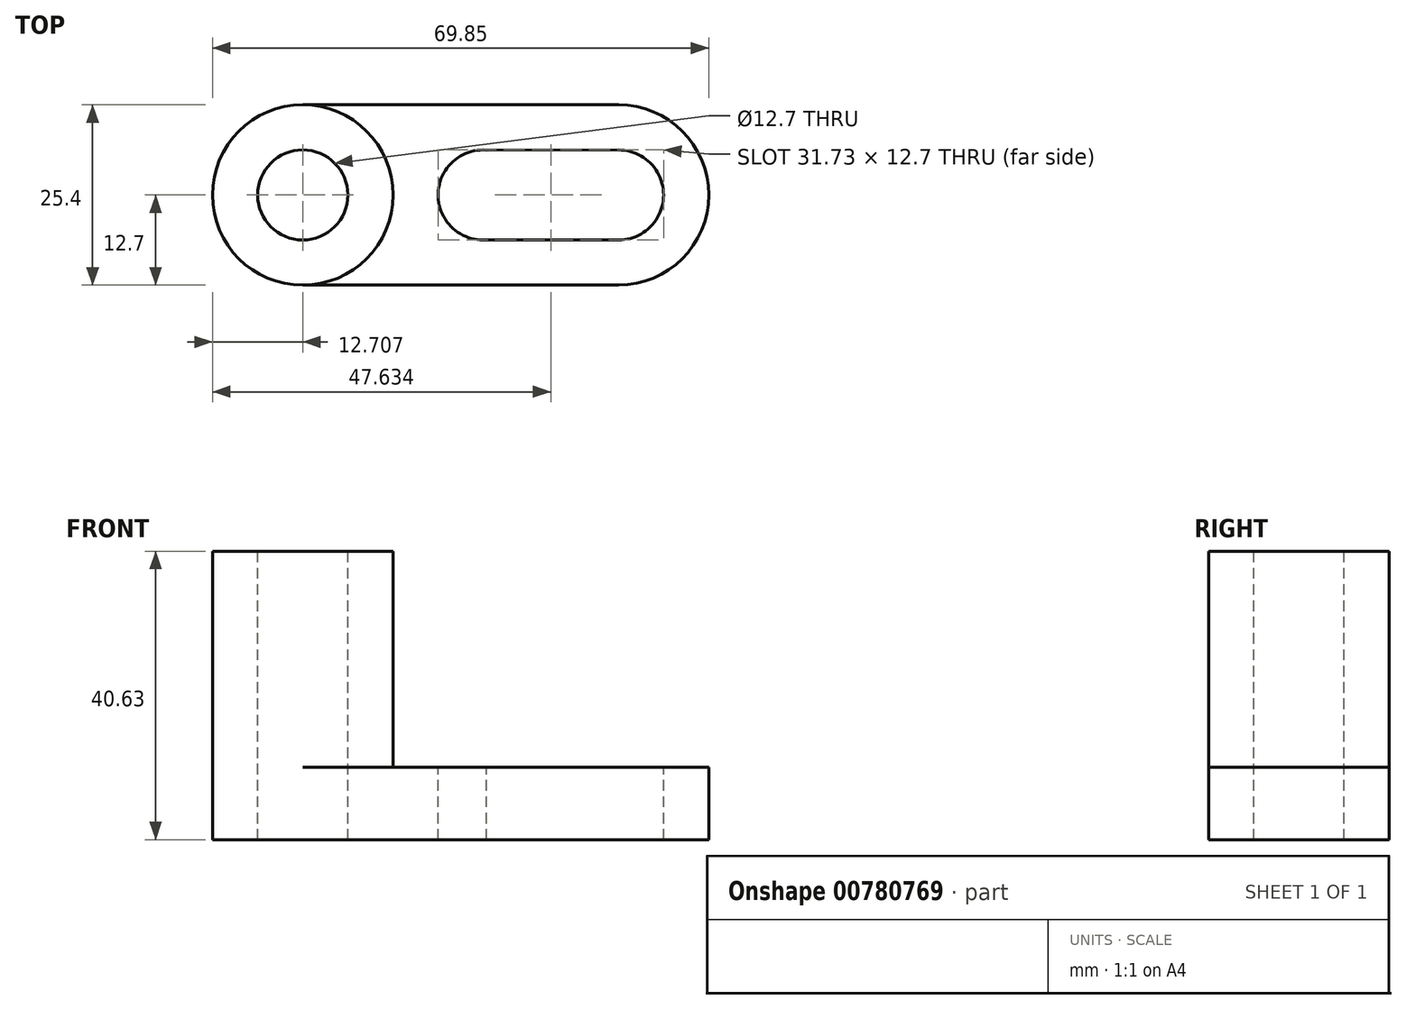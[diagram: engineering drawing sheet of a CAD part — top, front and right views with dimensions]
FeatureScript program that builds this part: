
annotation { "Feature Type Name" : "Feature", "Feature Type Description" : "" }
export const myFeature = defineFeature(function(context is Context, id is Id, definition is map)
    precondition{}
    {
        {
            var Q0;
            Q0=qCreatedBy(makeId("Front.planeOp"),FACE);
            var sketch = newSketch(context, id + "F0", { "sketchPlane" : qUnion([Q0])});
            skLineSegment(sketch, "E0", {"start": v(0, 0) * mm, "end": v(69.85, 0) * mm});
            skLineSegment(sketch, "E1", {"start": v(69.85, 0) * mm, "end": v(69.85, 10.2) * mm});
            skLineSegment(sketch, "E2", {"start": v(69.85, 10.2) * mm, "end": v(25.41, 10.2) * mm});
            skLineSegment(sketch, "E3", {"start": v(25.41, 10.2) * mm, "end": v(25.41, 40.63) * mm});
            skLineSegment(sketch, "E4", {"start": v(25.41, 40.63) * mm, "end": v(0, 40.63) * mm});
            skLineSegment(sketch, "E5", {"start": v(0, 40.63) * mm, "end": v(0, 0) * mm});
            skSolve(sketch);
        }
        {
            var Q0;
            Q0=makeQuery(id+"F0.imprint","IMPRINT",FACE,{"disambiguationData":[TD([[makeQuery(id+"F0.imprint","IMPRINT",EDGE,{"derivedFrom":sQuery(id+"F0.wireOp",EDGE,"E0")}),1.0]])]});
            extrude(context, id + "F1", {"entities" : qUnion([Q0]), "depth" : 25.4 * mm, "offsetDistance" : 25.4 * mm});
        }
        {
            var Q0;
            Q0=makeQuery(id+"F1.opExtrude","SWEPT_FACE",FACE,{"disambiguationData":[OSD([sQuery(id+"F0.wireOp",EDGE,"E4")])]});
            var sketch = newSketch(context, id + "F2", { "sketchPlane" : qUnion([Q0])});
            skCircle(sketch, "E6", {"center": v(12.7, -12.7) * mm, "radius": 6.35 * mm});
            skPoint(sketch, "E6.centerSnap0", {"position": v(0, -12.7) * mm});
            skPoint(sketch, "E6.centerSnap1", {"position": v(12.7, -25.4) * mm});
            skSolve(sketch);
        }
        {
            var Q0;
            Q0=makeQuery(id+"F2.imprint","IMPRINT",FACE,{"disambiguationData":[TD([[makeQuery(id+"F2.imprint","IMPRINT",EDGE,{"derivedFrom":sQuery(id+"F2.wireOp",EDGE,"E6")}),1.0]])]});
            extrude(context, id + "F3", {"entities" : qUnion([Q0]), "operationType" : NewBodyOperationType.REMOVE, "oppositeDirection" : true, "depth" : 50.8 * mm, "offsetDistance" : 25.4 * mm});
        }
        {
            var Q0;
            Q0=makeQuery(id+"F1.opExtrude","CAP_EDGE",EDGE,{"disambiguationData":[OSD([sQuery(id+"F0.wireOp",EDGE,"E3")])],"isStart":false});
            var Q1;
            Q1=makeQuery(id+"F1.opExtrude","CAP_EDGE",EDGE,{"disambiguationData":[OSD([sQuery(id+"F0.wireOp",EDGE,"E3")])],"isStart":true});
            var Q2;
            Q2=makeQuery(id+"F1.opExtrude","CAP_EDGE",EDGE,{"disambiguationData":[OSD([sQuery(id+"F0.wireOp",EDGE,"E5")])],"isStart":false});
            var Q3;
            Q3=makeQuery(id+"F1.opExtrude","CAP_EDGE",EDGE,{"disambiguationData":[OSD([sQuery(id+"F0.wireOp",EDGE,"E5")])],"isStart":true});
            var Q4;
            Q4=makeQuery(id+"F1.opExtrude","CAP_EDGE",EDGE,{"disambiguationData":[OSD([sQuery(id+"F0.wireOp",EDGE,"E1")])],"isStart":false});
            var Q5;
            Q5=makeQuery(id+"F1.opExtrude","CAP_EDGE",EDGE,{"disambiguationData":[OSD([sQuery(id+"F0.wireOp",EDGE,"E1")])],"isStart":true});
            fillet(context, id + "F4", {"entities" : qUnion([Q0, Q1, Q2, Q3, Q4, Q5]), "radius" : 12.7 * mm, "tangentPropagation" : true, "allowEdgeOverflow" : false});
        }
        {
            var Q0;
            Q0=makeQuery(id+"F1.opExtrude","SWEPT_FACE",FACE,{"disambiguationData":[OSD([sQuery(id+"F0.wireOp",EDGE,"E2")])]});
            var sketch = newSketch(context, id + "F5", { "sketchPlane" : qUnion([Q0])});
            skCircle(sketch, "E7", {"center": v(38.11, -12.7) * mm, "radius": 6.35 * mm});
            skCircle(sketch, "E8", {"center": v(57.15, -12.7) * mm, "radius": 6.35 * mm});
            skLineSegment(sketch, "E9", {"start": v(37.67, -6.37) * mm, "end": v(57.14, -6.35) * mm});
            skLineSegment(sketch, "E10", {"start": v(38.11, -19.05) * mm, "end": v(57.15, -19.05) * mm});
            skSolve(sketch);
        }
        {
            var Q0;
            Q0 = qSketchRegion(id + "F5", true);
            extrude(context, id + "F6", {"entities" : qUnion([Q0]), "operationType" : NewBodyOperationType.REMOVE, "oppositeDirection" : true, "depth" : 25.4 * mm, "offsetDistance" : 25.4 * mm});
        }
    });
